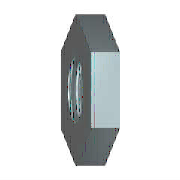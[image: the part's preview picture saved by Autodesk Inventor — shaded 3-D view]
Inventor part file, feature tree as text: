
AUTODESK INVENTOR PART (.ipt)
format: ipt  version: 2018 (Build 220112000, 112)  size: 131,584 bytes
history: native  units: mm (DEFAULTED — no unit token found)
features: other x4, sketch x2, extrude x1, chamfer x1
ambient origin geometry x8: Origin, YZ Plane, XZ Plane, XY Plane, X Axis, Y Axis, Z Axis, Center Point
bodies: Solid1 (feature_tree)
feature tree (8):
  extrude  "Extrusion1"  TaperAngle=0.0deg  [1 undecoded]
  other  "MSC_A1"
  other  "MSC_PT1"
  other  "MSC_PT2"
  other  "MSC_PF1"
  chamfer  "Chamfer1"  [1 undecoded]
  sketch  "Sketch1"  dims[d2=0.0mm]
  sketch  "Sketch2"  dims[d3=2.459mm d4=1.8mm d5=4.0mm d6=2.0mm d7=60.0deg d8=8.0mm d9=20.594885mm d14=0.0mm d15=0.0mm d16=0.0mm d17=0.3mm d18=0.3mm d20=45.0deg d21=0.0mm d23=0.0mm d24=0.0mm d25=0.0mm]
note: 2 required parameter values undecoded (feature->parameter linkage not recoverable at this tier; creation-order binding heuristic only, values carry confidence <= 0.55)
